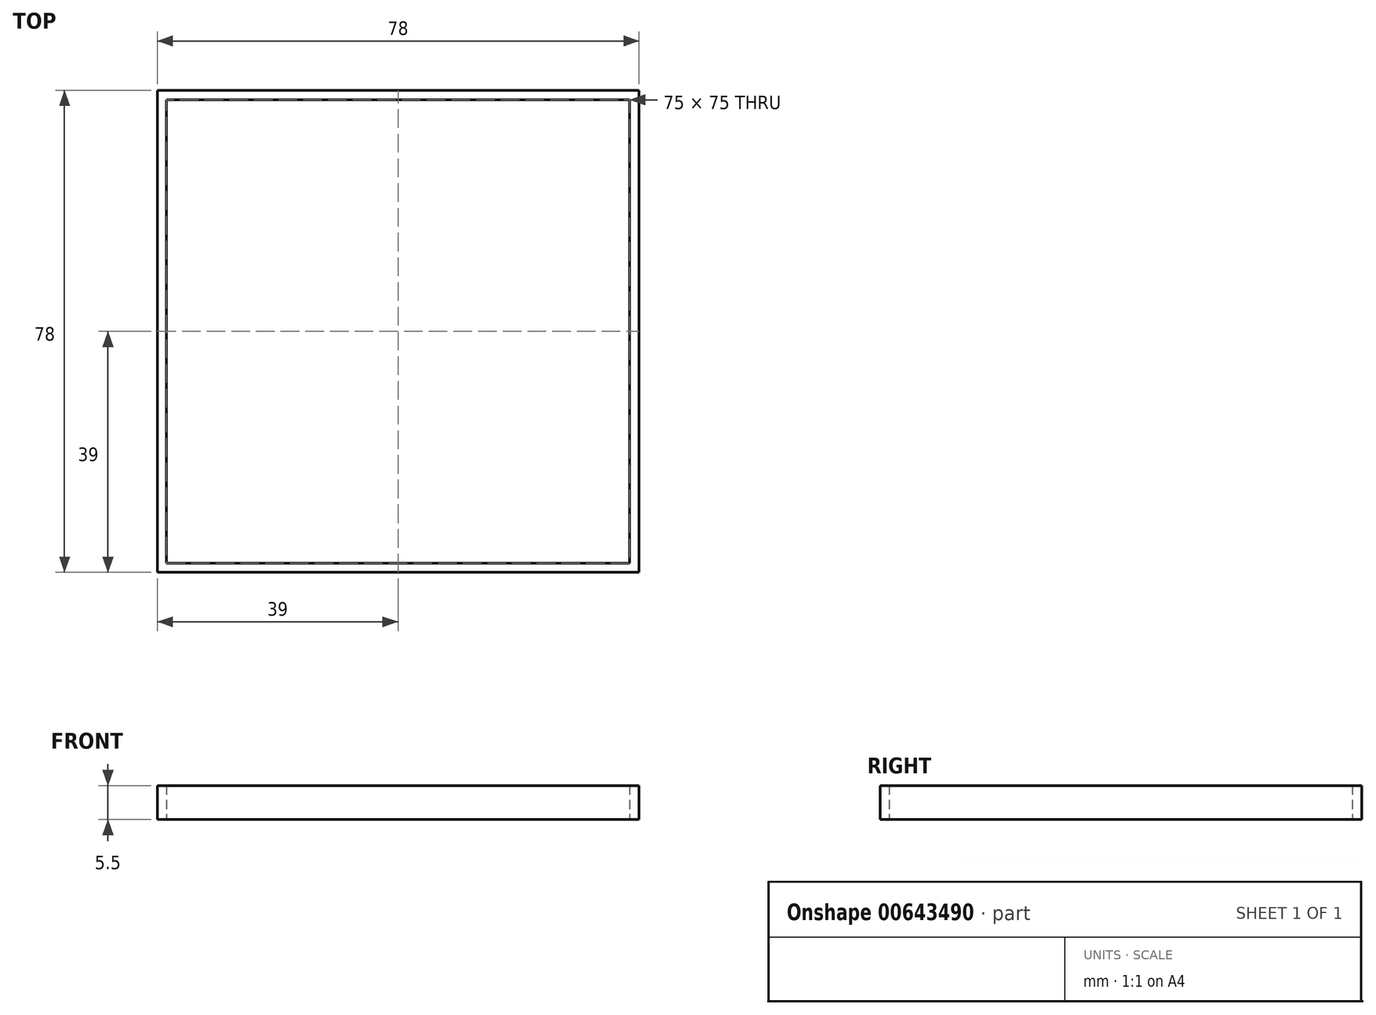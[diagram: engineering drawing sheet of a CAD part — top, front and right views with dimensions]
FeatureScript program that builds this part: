
annotation { "Feature Type Name" : "Feature", "Feature Type Description" : "" }
export const myFeature = defineFeature(function(context is Context, id is Id, definition is map)
    precondition{}
    {
        {
            var Q0;
            Q0=qCreatedBy(makeId("Top.planeOp"),FACE);
            var sketch = newSketch(context, id + "F0", { "sketchPlane" : qUnion([Q0])});
            skLineSegment(sketch, "E0.bottom", {"start": v(37.5, -37.5) * mm, "end": v(-37.5, -37.5) * mm});
            skLineSegment(sketch, "E0.top", {"start": v(37.5, 37.5) * mm, "end": v(-37.5, 37.5) * mm});
            skLineSegment(sketch, "E0.left", {"start": v(37.5, -37.5) * mm, "end": v(37.5, 37.5) * mm});
            skLineSegment(sketch, "E0.right", {"start": v(-37.5, -37.5) * mm, "end": v(-37.5, 37.5) * mm});
            skPoint(sketch, "E0.middle", {"position": v(0, 0) * mm});
            skLineSegment(sketch, "E1.bottom", {"start": v(39, -39) * mm, "end": v(-39, -39) * mm});
            skLineSegment(sketch, "E1.top", {"start": v(39, 39) * mm, "end": v(-39, 39) * mm});
            skLineSegment(sketch, "E1.left", {"start": v(39, -39) * mm, "end": v(39, 39) * mm});
            skLineSegment(sketch, "E1.right", {"start": v(-39, -39) * mm, "end": v(-39, 39) * mm});
            skSolve(sketch);
        }
        {
            var Q0;
            Q0=qSketchRegion(id+"F0",true);
            extrude(context, id + "F1", {"entities" : qUnion([Q0]), "depth" : 5.5 * mm, "offsetDistance" : 25 * mm});
        }
    });
